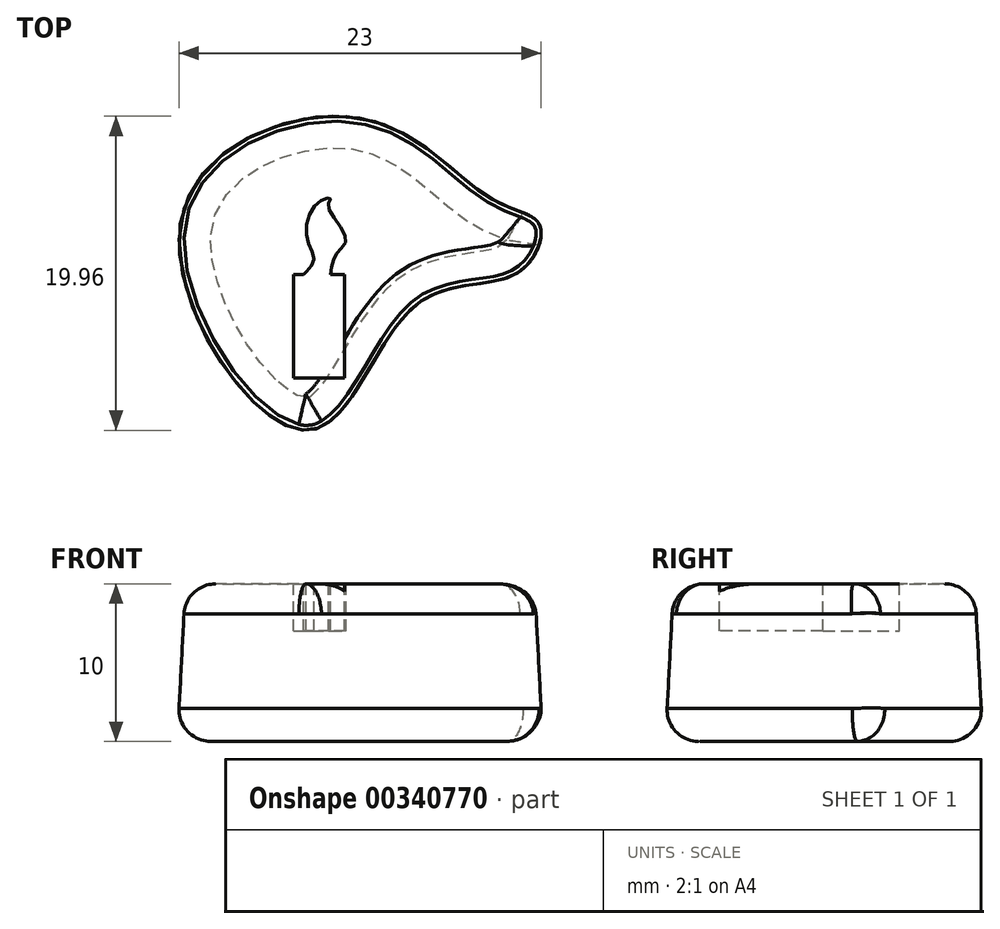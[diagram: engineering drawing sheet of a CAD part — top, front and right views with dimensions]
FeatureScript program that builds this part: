
annotation { "Feature Type Name" : "Feature", "Feature Type Description" : "" }
export const myFeature = defineFeature(function(context is Context, id is Id, definition is map)
    precondition{}
    {
        {
            var Q0;
            Q0=qCreatedBy(makeId("Top.planeOp"),FACE);
            var sketch = newSketch(context, id + "F0", { "sketchPlane" : qUnion([Q0])});
            skLineSegment(sketch, "E0.bottom", {"start": v(254, -266.7) * mm, "end": v(-254, -266.7) * mm, "construction": true});
            skLineSegment(sketch, "E0.top", {"start": v(254, 266.7) * mm, "end": v(-254, 266.7) * mm, "construction": true});
            skLineSegment(sketch, "E0.left", {"start": v(254, -266.7) * mm, "end": v(254, 266.7) * mm, "construction": true});
            skLineSegment(sketch, "E0.right", {"start": v(-254, -266.7) * mm, "end": v(-254, 266.7) * mm, "construction": true});
            skPoint(sketch, "E0.middle", {"position": v(0, 0) * mm});
            skLineSegment(sketch, "E1.bottom", {"start": v(10, 10) * mm, "end": v(-10, 10) * mm, "construction": true});
            skLineSegment(sketch, "E1.top", {"start": v(10, -10) * mm, "end": v(-10, -10) * mm, "construction": true});
            skLineSegment(sketch, "E1.left", {"start": v(10, 10) * mm, "end": v(10, -10) * mm, "construction": true});
            skLineSegment(sketch, "E1.right", {"start": v(-10, 10) * mm, "end": v(-10, -10) * mm, "construction": true});
            skPoint(sketch, "E2.4.internal.snap0", {"position": v(10, 0) * mm});
            skFitSpline(sketch, "E2", {"points": [v(1.74, 10) * mm, v(-10, 3.38) * mm, v(-1.81, -10) * mm, v(5.08, -2.05) * mm, v(11.55, 0) * mm, v(13.01, 3.17) * mm, v(10, 4.84) * mm, v(1.74, 10) * mm]});
            skSolve(sketch);
        }
        {
            var Q0;
            Q0 = qSketchRegion(id + "F0", true);
            extrude(context, id + "F1", {"entities" : qUnion([Q0]), "depth" : 10 * mm, "hasDraft" : true, "draftAngle" : 3 * degree, "draftPullDirection" : true});
        }
        {
            var Q0;
            Q0=makeQuery(id+"F1.opExtrude","CAP_EDGE",EDGE,{"disambiguationData":[OSD([sQuery(id+"F0.wireOp",EDGE,"E2")])],"isStart":true});
            var Q1;
            Q1=makeQuery(id+"F1.opExtrude","CAP_EDGE",EDGE,{"disambiguationData":[OSD([sQuery(id+"F0.wireOp",EDGE,"E2")])],"isStart":false});
            fillet(context, id + "F2", {"entities" : qUnion([Q0, Q1]), "radius" : 2 * mm, "tangentPropagation" : true, "allowEdgeOverflow" : false});
        }
        {
            var Q0;
            Q0=makeQuery(id+"F1.opExtrude","CAP_FACE",FACE,{"disambiguationData":[OSD([sQuery(id+"F0.wireOp",EDGE,"E2")])],"isStart":false});
            var sketch = newSketch(context, id + "F3", { "sketchPlane" : qUnion([Q0])});
            skLineSegment(sketch, "E3.bottom", {"start": v(-2.7, 0) * mm, "end": v(-2.08, 0) * mm});
            skLineSegment(sketch, "E3.top", {"start": v(-2.7, -6.57) * mm, "end": v(0.53, -6.57) * mm});
            skLineSegment(sketch, "E3.left", {"start": v(-2.7, 0) * mm, "end": v(-2.7, -6.57) * mm});
            skLineSegment(sketch, "E3.right", {"start": v(0.53, 0) * mm, "end": v(0.53, -6.57) * mm});
            skFitSpline(sketch, "E4", {"points": [v(-0.39, 0) * mm, v(0, 1.3) * mm, v(0.6, 2.3) * mm, v(-0.51, 4.33) * mm, v(-0.39, 4.83) * mm, v(-1.21, 4.54) * mm, v(-1.88, 2.34) * mm, v(-1.46, 0.77) * mm, v(-2.08, 0) * mm, v(-2.04, 0) * mm], "startDerivative": vector(1.5, 11.38) * mm, "endDerivative": vector(2.87, 0.61) * mm});
            skLineSegment(sketch, "E5.trimOffspring", {"start": v(-0.39, 0) * mm, "end": v(0.53, 0) * mm});
            skSolve(sketch);
        }
        {
            var Q0;
            Q0 = qSketchRegion(id + "F3", true);
            extrude(context, id + "F4", {"entities" : qUnion([Q0]), "operationType" : NewBodyOperationType.REMOVE, "oppositeDirection" : true, "depth" : 3 * mm});
        }
    });
